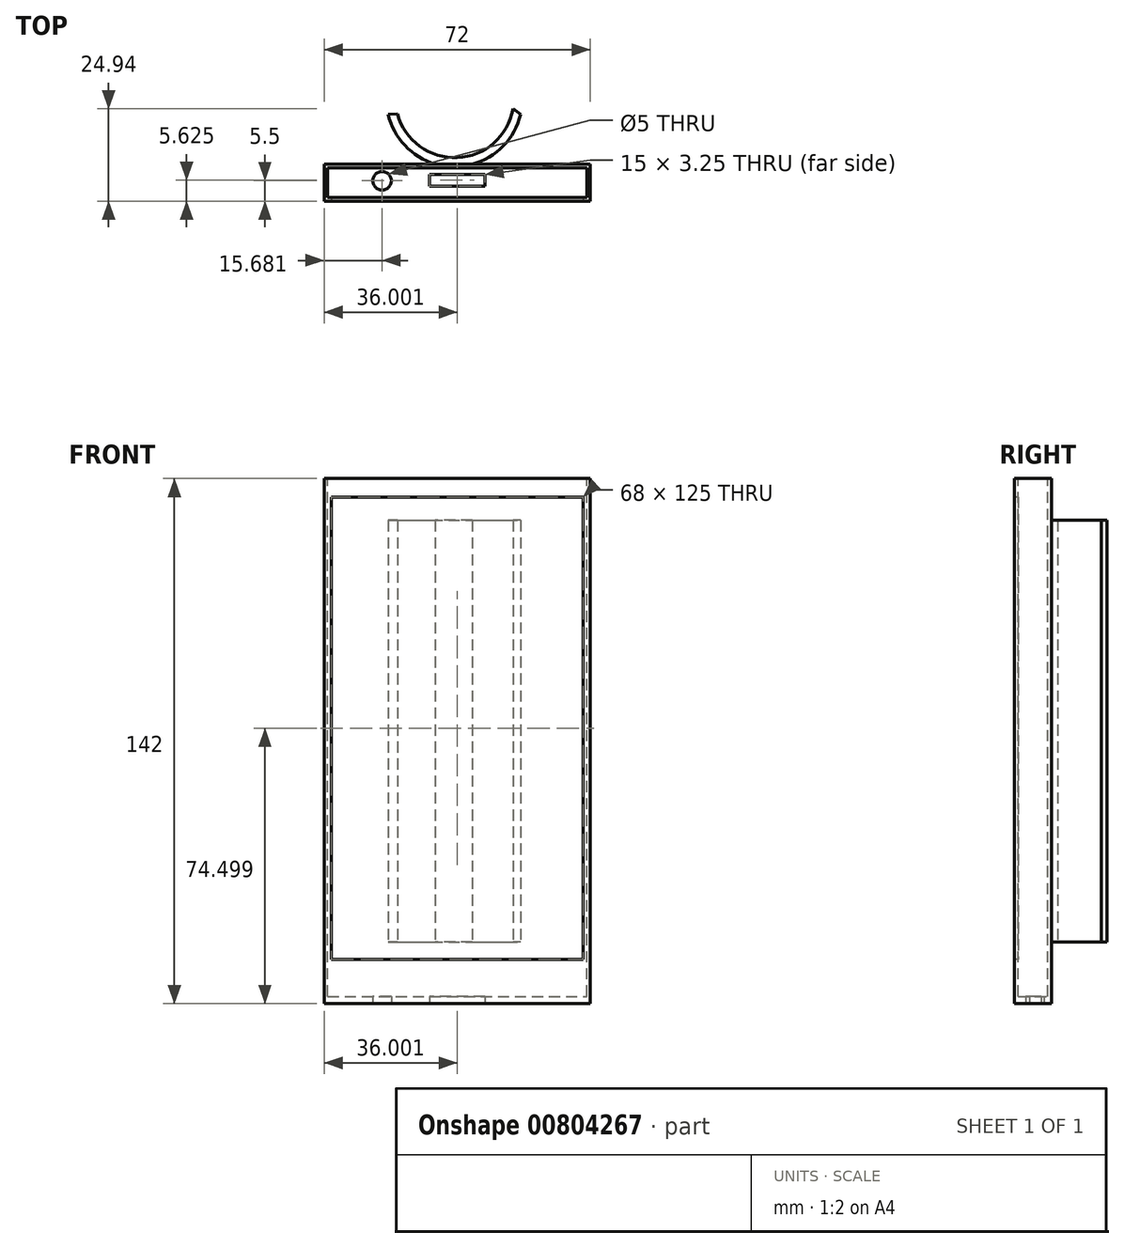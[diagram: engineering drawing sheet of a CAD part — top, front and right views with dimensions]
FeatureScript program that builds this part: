
annotation { "Feature Type Name" : "Feature", "Feature Type Description" : "" }
export const myFeature = defineFeature(function(context is Context, id is Id, definition is map)
    precondition{}
    {
        {
            var Q0;
            Q0=qCreatedBy(makeId("Front.planeOp"),FACE);
            var sketch = newSketch(context, id + "F0", { "sketchPlane" : qUnion([Q0])});
            skLineSegment(sketch, "E0.bottom", {"start": v(-48.56, 68.3) * mm, "end": v(23.44, 68.3) * mm});
            skLineSegment(sketch, "E0.top", {"start": v(-48.56, -73.7) * mm, "end": v(23.44, -73.7) * mm});
            skLineSegment(sketch, "E0.left", {"start": v(-48.56, 68.3) * mm, "end": v(-48.56, -73.7) * mm});
            skLineSegment(sketch, "E0.right", {"start": v(23.44, 68.3) * mm, "end": v(23.44, -73.7) * mm});
            skPoint(sketch, "E1", {"position": v(-12.56, 68.3) * mm});
            skSolve(sketch);
        }
        {
            var Q0;
            Q0 = qSketchRegion(id + "F0", true);
            extrude(context, id + "F1", {"entities" : qUnion([Q0]), "depth" : 10 * mm, "offsetDistance" : 25 * mm});
        }
        {
            var Q0;
            Q0=makeQuery(id+"F1.opExtrude","SWEPT_FACE",FACE,{"disambiguationData":[OSD([sQuery(id+"F0.wireOp",EDGE,"E0.bottom")])]});
            var sketch = newSketch(context, id + "F2", { "sketchPlane" : qUnion([Q0])});
            skLineSegment(sketch, "E2.bottom", {"start": v(-47.56, -9) * mm, "end": v(22.44, -9) * mm});
            skLineSegment(sketch, "E2.top", {"start": v(-47.56, -1) * mm, "end": v(22.44, -1) * mm});
            skLineSegment(sketch, "E2.left", {"start": v(-47.56, -9) * mm, "end": v(-47.56, -1) * mm});
            skLineSegment(sketch, "E2.right", {"start": v(22.44, -9) * mm, "end": v(22.44, -1) * mm});
            skSolve(sketch);
        }
        {
            var Q0;
            Q0 = qSketchRegion(id + "F2", true);
            extrude(context, id + "F3", {"entities" : qUnion([Q0]), "operationType" : NewBodyOperationType.REMOVE, "oppositeDirection" : true, "depth" : 140 * mm, "offsetDistance" : 25 * mm});
        }
        {
            var Q0;
            Q0=makeQuery(id+"F1.opExtrude","CAP_FACE",FACE,{"disambiguationData":[OSD([sQuery(id+"F0.wireOp",EDGE,"E0.bottom"),sQuery(id+"F0.wireOp",EDGE,"E0.top"),sQuery(id+"F0.wireOp",EDGE,"E0.left"),sQuery(id+"F0.wireOp",EDGE,"E0.right")])],"isStart":false});
            var sketch = newSketch(context, id + "F4", { "sketchPlane" : qUnion([Q0])});
            skLineSegment(sketch, "E3.bottom", {"start": v(-46.56, 63.3) * mm, "end": v(21.44, 63.3) * mm});
            skLineSegment(sketch, "E3.top", {"start": v(-46.56, -61.7) * mm, "end": v(21.44, -61.7) * mm});
            skLineSegment(sketch, "E3.left", {"start": v(-46.56, 63.3) * mm, "end": v(-46.56, -61.7) * mm});
            skLineSegment(sketch, "E3.right", {"start": v(21.44, 63.3) * mm, "end": v(21.44, -61.7) * mm});
            skSolve(sketch);
        }
        {
            var Q0;
            Q0 = qSketchRegion(id + "F4", true);
            extrude(context, id + "F5", {"entities" : qUnion([Q0]), "operationType" : NewBodyOperationType.REMOVE, "oppositeDirection" : true, "depth" : 4 * mm, "offsetDistance" : 25 * mm});
        }
        {
            var Q0;
            Q0=makeQuery(id+"F1.opExtrude","SWEPT_FACE",FACE,{"disambiguationData":[OSD([sQuery(id+"F0.wireOp",EDGE,"E0.top")])]});
            var sketch = newSketch(context, id + "F6", { "sketchPlane" : qUnion([Q0])});
            skLineSegment(sketch, "E4.bottom", {"start": v(-20.06, 6) * mm, "end": v(-5.06, 6) * mm});
            skLineSegment(sketch, "E4.top", {"start": v(-20.06, 2.75) * mm, "end": v(-5.06, 2.75) * mm});
            skLineSegment(sketch, "E4.left", {"start": v(-20.06, 6) * mm, "end": v(-20.06, 2.75) * mm});
            skLineSegment(sketch, "E4.right", {"start": v(-5.06, 6) * mm, "end": v(-5.06, 2.75) * mm});
            skCircle(sketch, "E5", {"center": v(-32.88, 4.5) * mm, "radius": 2.5 * mm});
            skPoint(sketch, "E6.orphan", {"position": v(0, 2.75) * mm});
            skSolve(sketch);
        }
        {
            var Q0;
            Q0 = qSketchRegion(id + "F6", true);
            extrude(context, id + "F7", {"entities" : qUnion([Q0]), "operationType" : NewBodyOperationType.REMOVE, "oppositeDirection" : true, "depth" : 5 * mm, "offsetDistance" : 25 * mm});
        }
        {
            var Q0;
            Q0=qCreatedBy(makeId("Top.planeOp"),FACE);
            var sketch = newSketch(context, id + "F8", { "sketchPlane" : qUnion([Q0])});
            skArc(sketch, "E7", {"start": v(-23.5, 13.57) * mm, "mid": v(-7.34, 1.74) * mm, "end": v(7.71, 14.94) * mm});
            skArc(sketch, "E8.0", {"start": v(-26.04, 13.44) * mm, "mid": v(-21.49, 5.02) * mm, "end": v(-13.33, 0) * mm});
            skLineSegment(sketch, "E9", {"start": v(-23.5, 13.57) * mm, "end": v(-26.04, 13.44) * mm});
            skLineSegment(sketch, "E10", {"start": v(9.8, 13.48) * mm, "end": v(7.71, 14.94) * mm});
            skArc(sketch, "E11", {"start": v(-3.33, 0) * mm, "mid": v(5.1, 4.93) * mm, "end": v(9.8, 13.48) * mm});
            skLineSegment(sketch, "E12", {"start": v(-3.33, 0) * mm, "end": v(-13.23, 0) * mm});
            skLineSegment(sketch, "E13", {"start": v(-3.33, 0) * mm, "end": v(-13.33, 0) * mm});
            skLineSegment(sketch, "E14", {"start": v(-13.33, 0) * mm, "end": v(-3.33, 0) * mm});
            skSolve(sketch);
        }
        {
            var Q0;
            Q0 = qSketchRegion(id + "F8", true);
            extrude(context, id + "F9", {"entities" : qUnion([Q0]), "endBound" : BoundingType.SYMMETRIC, "depth" : 114 * mm, "offsetDistance" : 25 * mm});
        }
        {
            var Q0;
            Q0=makeQuery(id+"F9.opExtrude","SWEPT_BODY",BODY,{"disambiguationData":[OSD([sQuery(id+"F8.wireOp",EDGE,"E7"),sQuery(id+"F8.wireOp",EDGE,"E8.0"),sQuery(id+"F8.wireOp",EDGE,"E9"),sQuery(id+"F8.wireOp",EDGE,"E10"),sQuery(id+"F8.wireOp",EDGE,"E11"),sQuery(id+"F8.wireOp",EDGE,"E14")])]});
            var Q1;
            Q1=makeQuery(id+"F1.opExtrude","CAP_EDGE",EDGE,{"disambiguationData":[OSD([sQuery(id+"F0.wireOp",EDGE,"E0.left")])],"isStart":true});
            transform(context, id + "F10", {"entities" : qUnion([Q0]), "transformType" : TransformType.TRANSLATION_3D, "dx" : -5.2 * mm, "dy" : 0 * mm, "dz" : 0 * mm, "makeCopy" : false});
        }
    });
